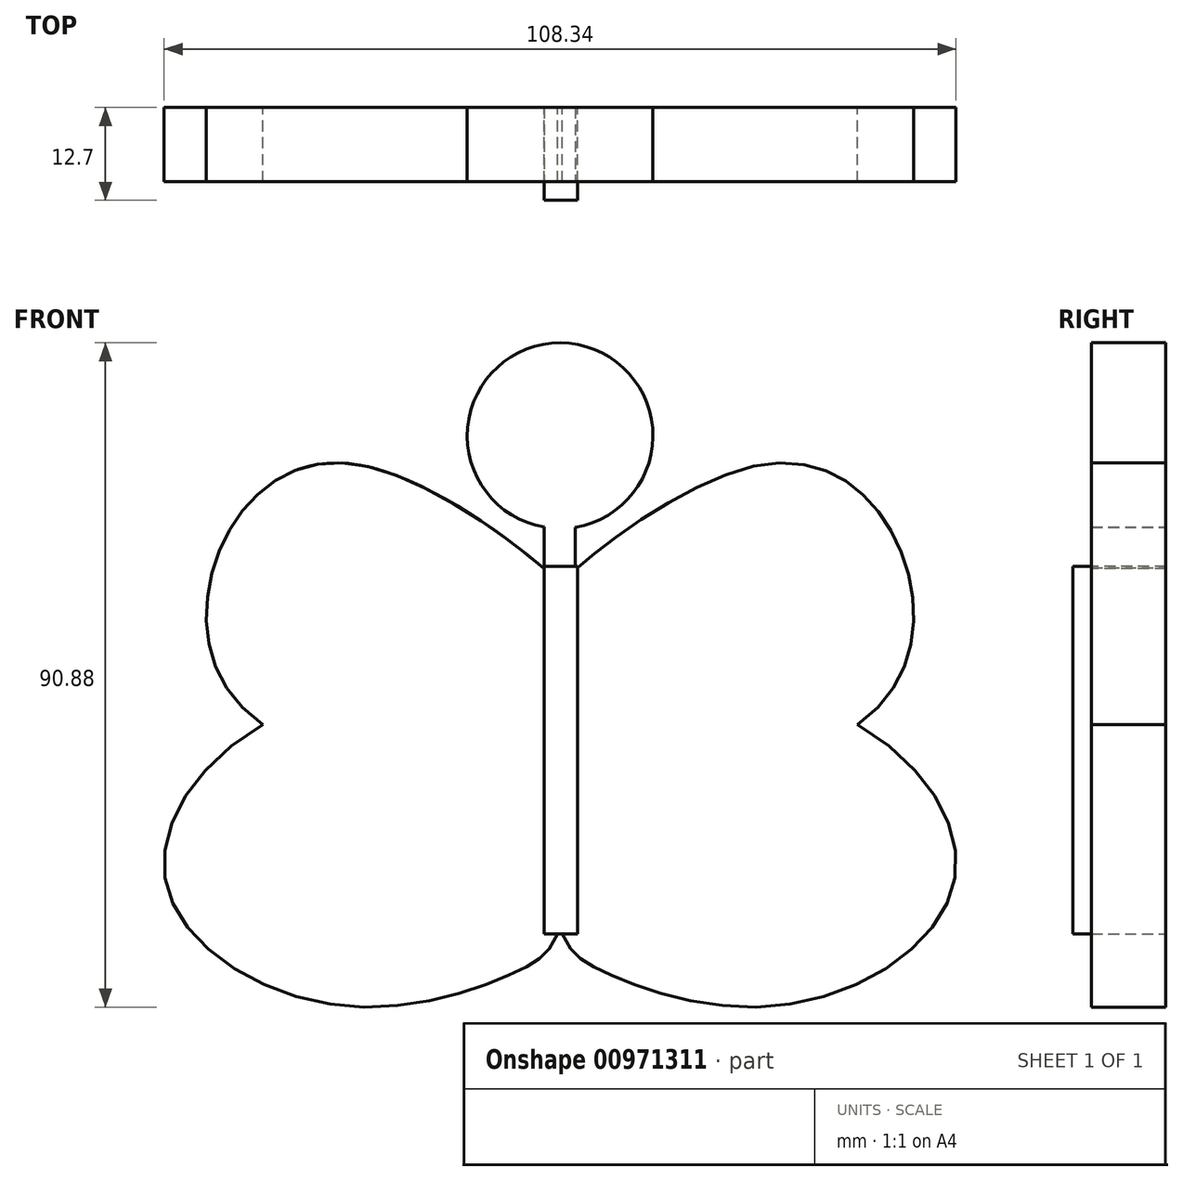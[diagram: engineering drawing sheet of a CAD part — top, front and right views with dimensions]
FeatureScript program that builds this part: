
annotation { "Feature Type Name" : "Feature", "Feature Type Description" : "" }
export const myFeature = defineFeature(function(context is Context, id is Id, definition is map)
    precondition{}
    {
        {
            var Q0;
            Q0=qCreatedBy(makeId("Front.planeOp"),FACE);
            var sketch = newSketch(context, id + "F0", { "sketchPlane" : qUnion([Q0])});
            skFitSpline(sketch, "E0", {"points": [v(-46.55, 22.47) * mm, v(-27.02, 34.03) * mm, v(0, 17.73) * mm, v(0, 17.35) * mm, v(0, 0) * mm, v(-40.67, -1.42) * mm, v(-46.55, 22.47) * mm]});
            skFitSpline(sketch, "E1.MirrorC", {"points": [v(46.55, 22.47) * mm, v(27.02, 34.03) * mm, v(0, 17.73) * mm, v(0, 17.35) * mm, v(0, 0) * mm, v(40.67, -1.42) * mm, v(46.55, 22.47) * mm]});
            skFitSpline(sketch, "E2", {"points": [v(-40.67, -1.42) * mm, v(-53.56, -24.36) * mm, v(-29.67, -39.91) * mm, v(-5.02, -34.8) * mm, v(0, -29.3) * mm, v(0, 0) * mm, v(-40.67, -1.42) * mm]});
            skFitSpline(sketch, "E3.MirrorC", {"points": [v(40.67, -1.42) * mm, v(53.56, -24.36) * mm, v(29.67, -39.91) * mm, v(5.02, -34.8) * mm, v(0, -29.3) * mm, v(0, 0) * mm, v(40.67, -1.42) * mm]});
            skSolve(sketch);
        }
        {
            var Q0;
            {var subQ0=sQuery(id+"F0.wireOp",EDGE,"E2");var subQ1=sQuery(id+"F0.wireOp",EDGE,"E0");var subQ2=makeQuery(id+"F0.imprint","INTERSECT",VERTEX,{"derivedFrom":[subQ1,subQ0]});Q0=makeQuery(id+"F0.imprint","IMPRINT",FACE,{"disambiguationData":[TD([[makeQuery(id+"F0.imprint","IMPRINT",EDGE,{"disambiguationData":[TD([[subQ2,1.0]])],"derivedFrom":subQ1}),1.0]])]});}
            var Q1;
            {var subQ0=sQuery(id+"F0.wireOp",EDGE,"E1.MirrorC");var subQ1=sQuery(id+"F0.wireOp",EDGE,"E0");var subQ2=makeQuery(id+"F0.imprint","INTERSECT",VERTEX,{"disambiguationData":[OD(0.0)],"derivedFrom":[subQ1,subQ0]});Q1=makeQuery(id+"F0.imprint","IMPRINT",FACE,{"disambiguationData":[TD([[makeQuery(id+"F0.imprint","IMPRINT",EDGE,{"disambiguationData":[TD([[subQ2,-1.0]])],"derivedFrom":subQ1}),1.0]])]});}
            var Q2;
            {var subQ0=sQuery(id+"F0.wireOp",EDGE,"E3.MirrorC");var subQ1=sQuery(id+"F0.wireOp",EDGE,"E1.MirrorC");var subQ2=makeQuery(id+"F0.imprint","INTERSECT",VERTEX,{"derivedFrom":[subQ1,subQ0]});Q2=makeQuery(id+"F0.imprint","IMPRINT",FACE,{"disambiguationData":[TD([[makeQuery(id+"F0.imprint","IMPRINT",EDGE,{"disambiguationData":[TD([[subQ2,1.0]])],"derivedFrom":subQ1}),-1.0]])]});}
            var Q3;
            {var subQ0=sQuery(id+"F0.wireOp",EDGE,"E2");var subQ1=sQuery(id+"F0.wireOp",EDGE,"E0");var subQ2=makeQuery(id+"F0.imprint","INTERSECT",VERTEX,{"derivedFrom":[subQ1,subQ0]});Q3=makeQuery(id+"F0.imprint","IMPRINT",FACE,{"disambiguationData":[TD([[makeQuery(id+"F0.imprint","IMPRINT",EDGE,{"disambiguationData":[TD([[subQ2,1.0]])],"derivedFrom":subQ1}),-1.0]])]});}
            var Q4;
            {var subQ0=sQuery(id+"F0.wireOp",EDGE,"E3.MirrorC");var subQ1=sQuery(id+"F0.wireOp",EDGE,"E1.MirrorC");var subQ2=makeQuery(id+"F0.imprint","INTERSECT",VERTEX,{"derivedFrom":[subQ1,subQ0]});Q4=makeQuery(id+"F0.imprint","IMPRINT",FACE,{"disambiguationData":[TD([[makeQuery(id+"F0.imprint","IMPRINT",EDGE,{"disambiguationData":[TD([[subQ2,1.0]])],"derivedFrom":subQ1}),1.0]])]});}
            var Q5;
            {var subQ0=sQuery(id+"F0.wireOp",EDGE,"E1.MirrorC");var subQ1=sQuery(id+"F0.wireOp",EDGE,"E0");var subQ2=makeQuery(id+"F0.imprint","INTERSECT",VERTEX,{"disambiguationData":[OD(0.0)],"derivedFrom":[subQ1,subQ0]});Q5=makeQuery(id+"F0.imprint","IMPRINT",FACE,{"disambiguationData":[TD([[makeQuery(id+"F0.imprint","IMPRINT",EDGE,{"disambiguationData":[TD([[subQ2,1.0]])],"derivedFrom":subQ1}),-1.0]])]});}
            var Q6;
            {var subQ0=sQuery(id+"F0.wireOp",EDGE,"E3.MirrorC");var subQ3=sQuery(id+"F0.wireOp",EDGE,"E2");var subQ7=makeQuery(id+"F0.imprint","INTERSECT",VERTEX,{"derivedFrom":[subQ3,subQ0]});Q6=makeQuery(id+"F0.imprint","IMPRINT",FACE,{"disambiguationData":[TD([[makeQuery(id+"F0.imprint","IMPRINT",EDGE,{"disambiguationData":[TD([[subQ7,-1.0]])],"derivedFrom":subQ3}),1.0]])]});}
            var Q7;
            {var subQ0=sQuery(id+"F0.wireOp",EDGE,"E1.MirrorC");var subQ1=sQuery(id+"F0.wireOp",EDGE,"E0");var subQ2=makeQuery(id+"F0.imprint","INTERSECT",VERTEX,{"disambiguationData":[OD(1.0)],"derivedFrom":[subQ1,subQ0]});Q7=makeQuery(id+"F0.imprint","IMPRINT",FACE,{"disambiguationData":[TD([[makeQuery(id+"F0.imprint","IMPRINT",EDGE,{"disambiguationData":[TD([[subQ2,-1.0]])],"derivedFrom":subQ1}),-1.0]])]});}
            var Q8;
            {var subQ0=sQuery(id+"F0.wireOp",EDGE,"E2");var subQ1=sQuery(id+"F0.wireOp",EDGE,"E1.MirrorC");var subQ2=makeQuery(id+"F0.imprint","INTERSECT",VERTEX,{"derivedFrom":[subQ1,subQ0]});Q8=makeQuery(id+"F0.imprint","IMPRINT",FACE,{"disambiguationData":[TD([[makeQuery(id+"F0.imprint","IMPRINT",EDGE,{"disambiguationData":[TD([[subQ2,1.0]])],"derivedFrom":subQ1}),1.0]])]});}
            var Q9;
            {var subQ0=sQuery(id+"F0.wireOp",EDGE,"E1.MirrorC");var subQ1=sQuery(id+"F0.wireOp",EDGE,"E0");var subQ2=makeQuery(id+"F0.imprint","INTERSECT",VERTEX,{"disambiguationData":[OD(0.0)],"derivedFrom":[subQ1,subQ0]});Q9=makeQuery(id+"F0.imprint","IMPRINT",FACE,{"disambiguationData":[TD([[makeQuery(id+"F0.imprint","IMPRINT",EDGE,{"disambiguationData":[TD([[subQ2,-1.0]])],"derivedFrom":subQ1}),-1.0]])]});}
            var Q10;
            {var subQ0=sQuery(id+"F0.wireOp",EDGE,"E3.MirrorC");var subQ1=sQuery(id+"F0.wireOp",EDGE,"E0");var subQ2=makeQuery(id+"F0.imprint","INTERSECT",VERTEX,{"derivedFrom":[subQ1,subQ0]});Q10=makeQuery(id+"F0.imprint","IMPRINT",FACE,{"disambiguationData":[TD([[makeQuery(id+"F0.imprint","IMPRINT",EDGE,{"disambiguationData":[TD([[subQ2,1.0]])],"derivedFrom":subQ1}),-1.0]])]});}
            extrude(context, id + "F1", {"entities" : qUnion([Q0, Q1, Q2, Q3, Q4, Q5, Q6, Q7, Q8, Q9, Q10]), "depth" : 10.16 * mm, "offsetDistance" : 25.4 * mm});
        }
        {
            var Q0;
            Q0=qCreatedBy(makeId("Front.planeOp"),FACE);
            var sketch = newSketch(context, id + "F2", { "sketchPlane" : qUnion([Q0])});
            skCircle(sketch, "E4", {"center": v(0, 38.1) * mm, "radius": 12.7 * mm});
            skLineSegment(sketch, "E5.bottom", {"start": v(-2.19, 29.06) * mm, "end": v(2.09, 29.06) * mm});
            skLineSegment(sketch, "E5.top", {"start": v(-2.19, 9.69) * mm, "end": v(2.09, 9.69) * mm});
            skLineSegment(sketch, "E5.left", {"start": v(-2.19, 29.06) * mm, "end": v(-2.19, 9.69) * mm});
            skLineSegment(sketch, "E5.right", {"start": v(2.09, 29.06) * mm, "end": v(2.09, 9.69) * mm});
            skSolve(sketch);
        }
        {
            var Q0;
            Q0 = qSketchRegion(id + "F2", true);
            extrude(context, id + "F3", {"entities" : qUnion([Q0]), "operationType" : NewBodyOperationType.ADD, "depth" : 10.16 * mm, "offsetDistance" : 25.4 * mm});
        }
        {
            var Q0;
            Q0=qCreatedBy(makeId("Front.planeOp"),FACE);
            var sketch = newSketch(context, id + "F4", { "sketchPlane" : qUnion([Q0])});
            skLineSegment(sketch, "E6.bottom", {"start": v(-2.18, 20.2) * mm, "end": v(0, 20.2) * mm});
            skLineSegment(sketch, "E6.top", {"start": v(-2.18, -30.05) * mm, "end": v(0, -30.05) * mm});
            skLineSegment(sketch, "E6.left", {"start": v(-2.18, 20.2) * mm, "end": v(-2.18, -30.05) * mm});
            skLineSegment(sketch, "E6.right", {"start": v(0, 20.2) * mm, "end": v(0, -30.05) * mm});
            skLineSegment(sketch, "E7.bottom", {"start": v(2.37, 20.2) * mm, "end": v(0, 20.2) * mm});
            skLineSegment(sketch, "E7.top", {"start": v(2.37, -30.05) * mm, "end": v(0, -30.05) * mm});
            skLineSegment(sketch, "E7.left", {"start": v(2.37, 20.2) * mm, "end": v(2.37, -30.05) * mm});
            skSolve(sketch);
        }
        {
            var Q0;
            Q0 = qSketchRegion(id + "F4", true);
            extrude(context, id + "F5", {"entities" : qUnion([Q0]), "operationType" : NewBodyOperationType.ADD, "depth" : 12.7 * mm, "offsetDistance" : 25.4 * mm});
        }
    });
